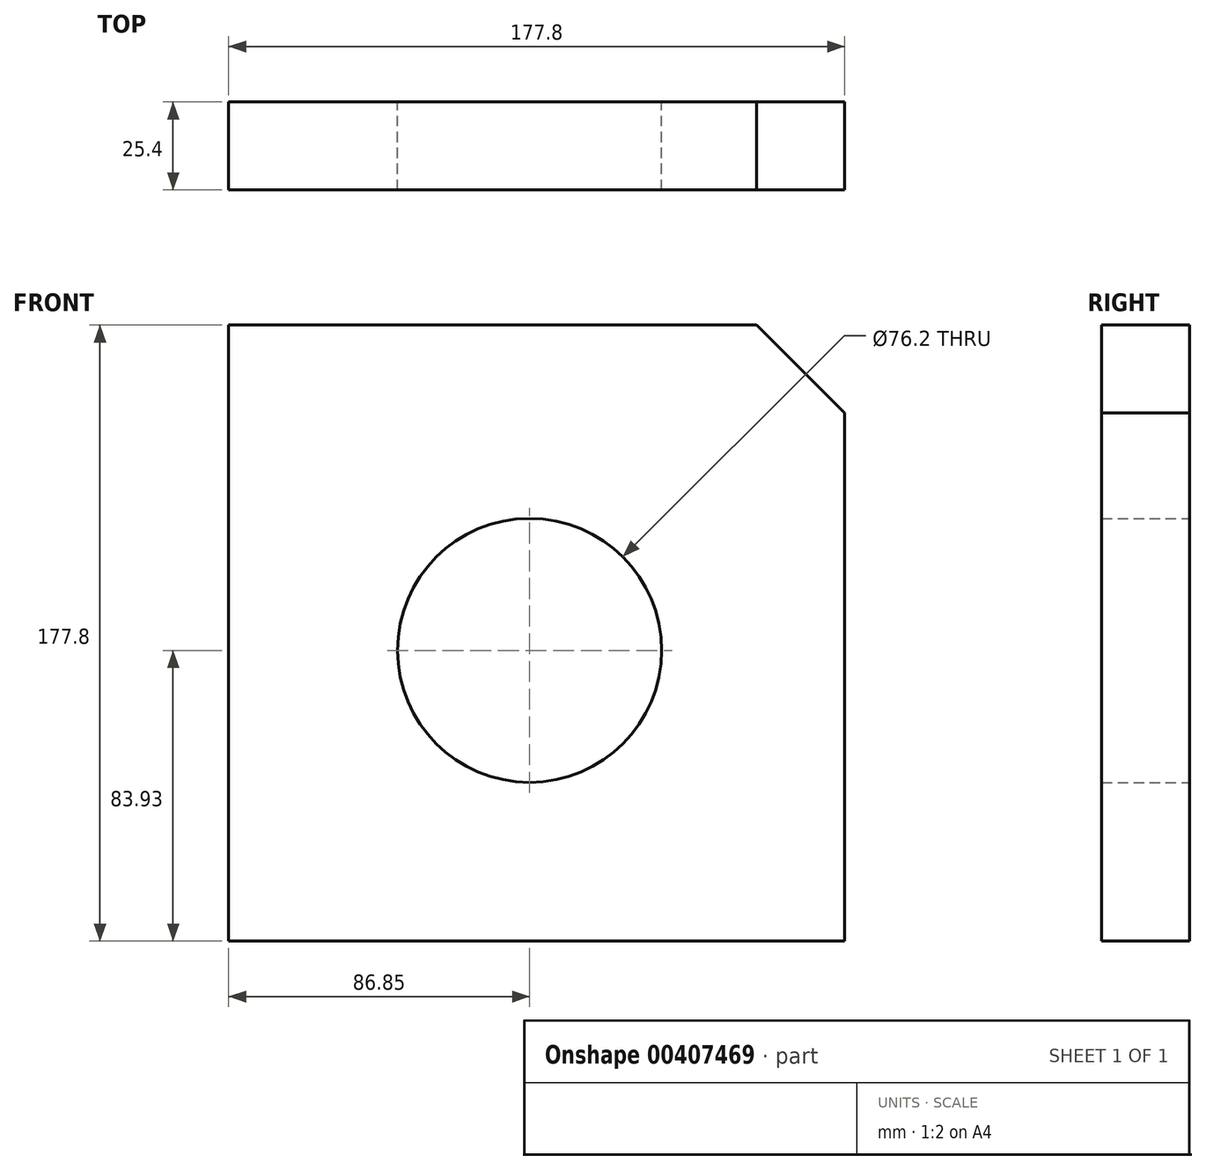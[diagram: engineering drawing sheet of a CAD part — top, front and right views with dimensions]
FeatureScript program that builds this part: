
annotation { "Feature Type Name" : "Feature", "Feature Type Description" : "" }
export const myFeature = defineFeature(function(context is Context, id is Id, definition is map)
    precondition{}
    {
        {
            var Q0;
            Q0=qCreatedBy(makeId("Front.planeOp"),FACE);
            var sketch = newSketch(context, id + "F0", { "sketchPlane" : qUnion([Q0])});
            skLineSegment(sketch, "E0.bottom", {"start": v(-86.85, 93.87) * mm, "end": v(90.95, 93.87) * mm});
            skLineSegment(sketch, "E0.top", {"start": v(-86.85, -83.93) * mm, "end": v(90.95, -83.93) * mm});
            skLineSegment(sketch, "E0.left", {"start": v(-86.85, 93.87) * mm, "end": v(-86.85, -83.93) * mm});
            skLineSegment(sketch, "E0.right", {"start": v(90.95, 93.87) * mm, "end": v(90.95, -83.93) * mm});
            skCircle(sketch, "E1", {"center": v(0, 0) * mm, "radius": 38.1 * mm});
            skSolve(sketch);
        }
        {
            var Q0;
            Q0 = qSketchRegion(id + "F0", true);
            extrude(context, id + "F1", {"entities" : qUnion([Q0]), "depth" : 25.4 * mm});
        }
        {
            var Q0;
            Q0=makeQuery(id+"F1.opExtrude","SWEPT_EDGE",EDGE,{"disambiguationData":[OSD([sQuery(id+"F0.wireOp",EDGE,"E0.bottom"),sQuery(id+"F0.wireOp",EDGE,"E0.right")])]});
            chamfer(context, id + "F2", {"entities" : qUnion([Q0]), "width" : 25.4 * mm, "tangentPropagation" : true});
        }
    });
